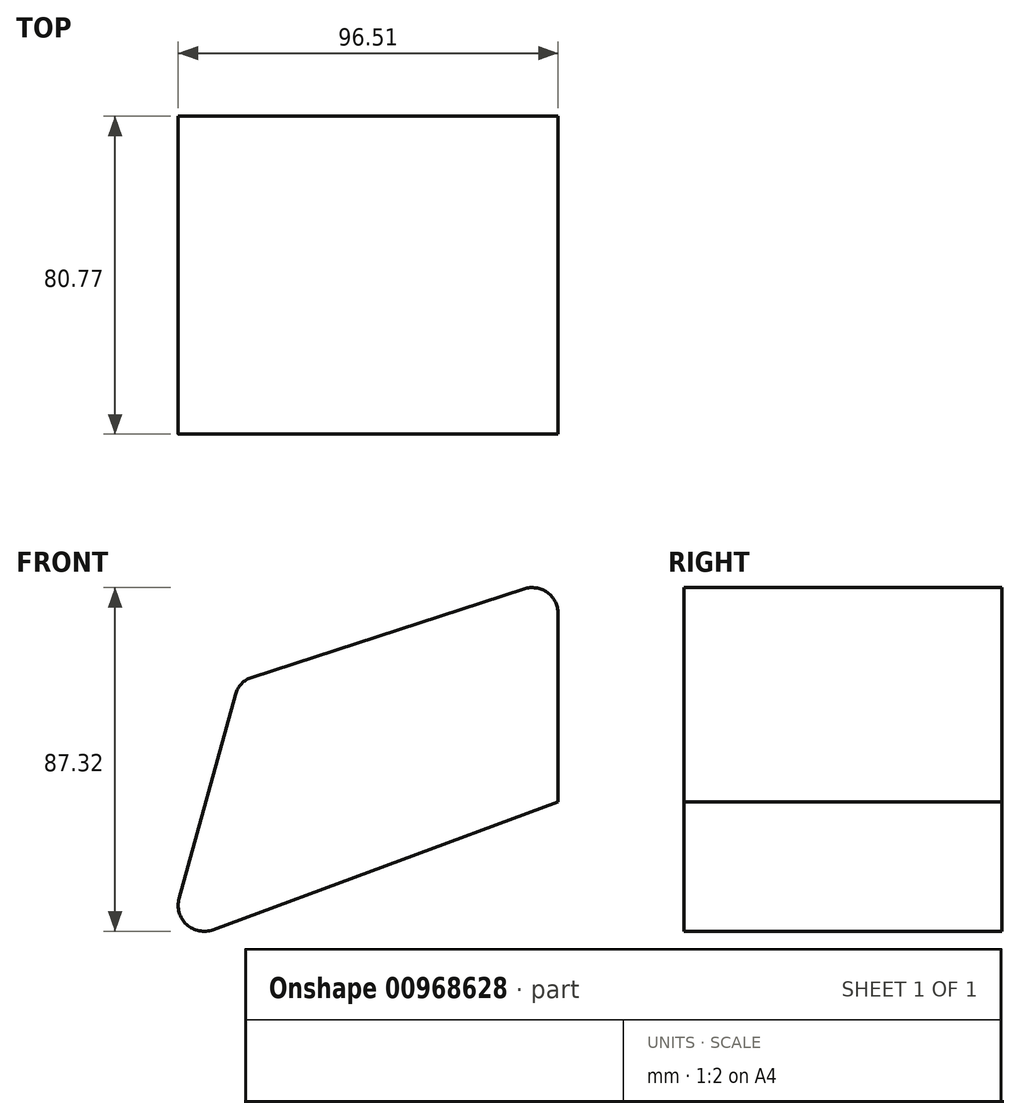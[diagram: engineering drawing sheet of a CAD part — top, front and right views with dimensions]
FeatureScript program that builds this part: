
annotation { "Feature Type Name" : "Feature", "Feature Type Description" : "" }
export const myFeature = defineFeature(function(context is Context, id is Id, definition is map)
    precondition{}
    {
        {
            var Q0;
            Q0=qCreatedBy(makeId("Front.planeOp"),FACE);
            var sketch = newSketch(context, id + "F0", { "sketchPlane" : qUnion([Q0])});
            skLineSegment(sketch, "E0", {"start": v(-36.02, 25.7) * mm, "end": v(-50.33, -26.16) * mm});
            skLineSegment(sketch, "E1", {"start": v(-41.69, -34.1) * mm, "end": v(45.95, -1.6) * mm});
            skLineSegment(sketch, "E2", {"start": v(45.95, -1.6) * mm, "end": v(45.95, 46.23) * mm});
            skLineSegment(sketch, "E3", {"start": v(37.33, 52.5) * mm, "end": v(-31.86, 30.05) * mm});
            skPoint(sketch, "E4.visualSharp", {"position": v(-35.11, 29) * mm});
            skArc(sketch, "E4.filletArc", {"start": v(-31.86, 30.05) * mm, "mid": v(-34.49, 28.4) * mm, "end": v(-36.02, 25.7) * mm});
            skPoint(sketch, "E5.visualSharp", {"position": v(45.95, 55.3) * mm});
            skArc(sketch, "E5.filletArc", {"start": v(45.95, 46.23) * mm, "mid": v(43.23, 51.56) * mm, "end": v(37.33, 52.5) * mm});
            skPoint(sketch, "E6.visualSharp", {"position": v(-53.75, -38.57) * mm});
            skArc(sketch, "E6.filletArc", {"start": v(-50.33, -26.16) * mm, "mid": v(-48.43, -32.77) * mm, "end": v(-41.69, -34.1) * mm});
            skSolve(sketch);
        }
        {
            var Q0;
            Q0=makeQuery(id+"F0.imprint","IMPRINT",FACE,{"disambiguationData":[TD([[makeQuery(id+"F0.imprint","IMPRINT",EDGE,{"derivedFrom":sQuery(id+"F0.wireOp",EDGE,"E0")}),1.0]])]});
            extrude(context, id + "F1", {"entities" : qUnion([Q0]), "depth" : 80.77 * mm, "offsetDistance" : 25.4 * mm});
        }
    });
